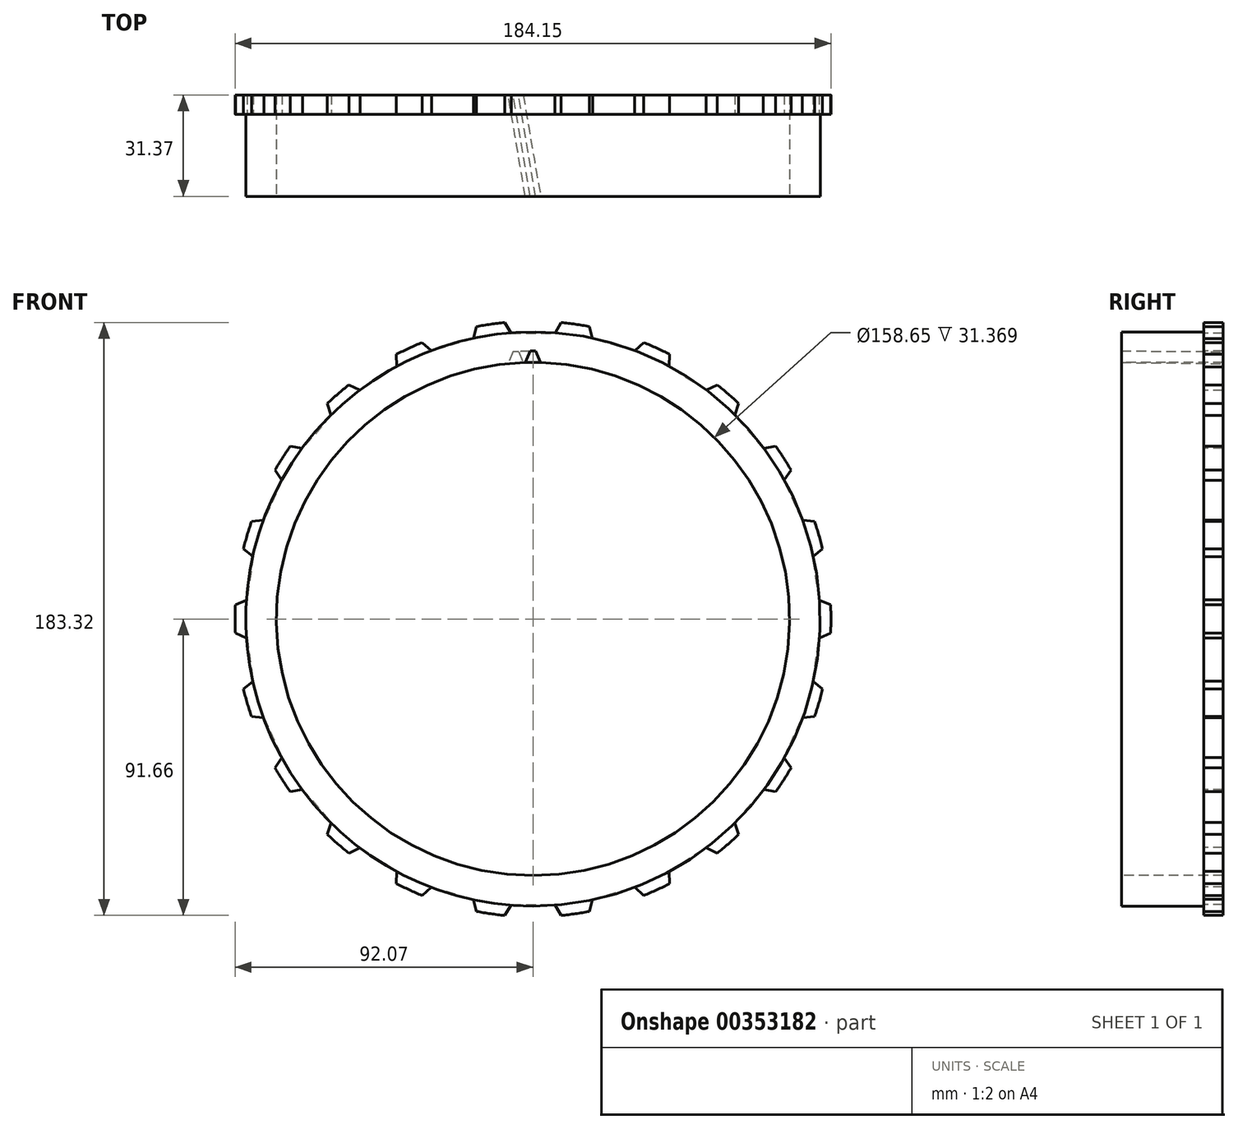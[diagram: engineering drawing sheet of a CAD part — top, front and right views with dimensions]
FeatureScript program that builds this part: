
annotation { "Feature Type Name" : "Feature", "Feature Type Description" : "" }
export const myFeature = defineFeature(function(context is Context, id is Id, definition is map)
    precondition{}
    {
        {
            var Q0;
            Q0=qCreatedBy(makeId("Front.planeOp"),FACE);
            var sketch = newSketch(context, id + "F0", { "sketchPlane" : qUnion([Q0])});
            skCircle(sketch, "E0", {"center": v(0, 0) * mm, "radius": 92.08 * mm});
            skCircle(sketch, "E1", {"center": v(0, 0) * mm, "radius": 79.32 * mm});
            skLineSegment(sketch, "E2", {"start": v(-6.74, 88.36) * mm, "end": v(0, 88.36) * mm});
            skLineSegment(sketch, "E3", {"start": v(-6.74, 88.36) * mm, "end": v(-8.72, 91.66) * mm});
            skLineSegment(sketch, "E4", {"start": v(0, 88.36) * mm, "end": v(0, 92.08) * mm});
            skLineSegment(sketch, "E5.MirrorCS", {"start": v(6.74, 88.36) * mm, "end": v(0, 88.36) * mm});
            skLineSegment(sketch, "E6.MirrorCS", {"start": v(6.74, 88.36) * mm, "end": v(8.72, 91.66) * mm});
            skLineSegment(sketch, "E7.1.0", {"start": v(-31.36, 82.88) * mm, "end": v(-34.2, 85.49) * mm});
            skLineSegment(sketch, "E7.1.1", {"start": v(-31.36, 82.88) * mm, "end": v(-24.9, 84.78) * mm});
            skLineSegment(sketch, "E7.1.2", {"start": v(-18.42, 86.68) * mm, "end": v(-24.9, 84.78) * mm});
            skLineSegment(sketch, "E7.1.3", {"start": v(-18.42, 86.68) * mm, "end": v(-17.45, 90.4) * mm});
            skLineSegment(sketch, "E7.2.0", {"start": v(-53.44, 70.69) * mm, "end": v(-56.9, 72.4) * mm});
            skLineSegment(sketch, "E7.2.1", {"start": v(-53.44, 70.69) * mm, "end": v(-47.77, 74.33) * mm});
            skLineSegment(sketch, "E7.2.2", {"start": v(-42.1, 77.98) * mm, "end": v(-47.77, 74.33) * mm});
            skLineSegment(sketch, "E7.2.3", {"start": v(-42.1, 77.98) * mm, "end": v(-42.22, 81.83) * mm});
            skLineSegment(sketch, "E7.3.0", {"start": v(-71.2, 52.77) * mm, "end": v(-74.99, 53.43) * mm});
            skLineSegment(sketch, "E7.3.1", {"start": v(-71.2, 52.77) * mm, "end": v(-66.78, 57.86) * mm});
            skLineSegment(sketch, "E7.3.2", {"start": v(-62.36, 62.96) * mm, "end": v(-66.78, 57.86) * mm});
            skLineSegment(sketch, "E7.3.3", {"start": v(-62.36, 62.96) * mm, "end": v(-63.56, 66.62) * mm});
            skLineSegment(sketch, "E7.4.0", {"start": v(-83.18, 30.57) * mm, "end": v(-87, 30.14) * mm});
            skLineSegment(sketch, "E7.4.1", {"start": v(-83.18, 30.57) * mm, "end": v(-80.37, 36.7) * mm});
            skLineSegment(sketch, "E7.4.2", {"start": v(-77.57, 42.84) * mm, "end": v(-80.37, 36.7) * mm});
            skLineSegment(sketch, "E7.4.3", {"start": v(-77.57, 42.84) * mm, "end": v(-79.75, 46.01) * mm});
            skLineSegment(sketch, "E7.5.0", {"start": v(-88.42, 5.9) * mm, "end": v(-91.97, 4.4) * mm});
            skLineSegment(sketch, "E7.5.1", {"start": v(-88.42, 5.9) * mm, "end": v(-87.46, 12.57) * mm});
            skLineSegment(sketch, "E7.5.2", {"start": v(-86.5, 19.25) * mm, "end": v(-87.46, 12.57) * mm});
            skLineSegment(sketch, "E7.5.3", {"start": v(-86.5, 19.25) * mm, "end": v(-89.49, 21.68) * mm});
            skLineSegment(sketch, "E7.6.0", {"start": v(-86.5, -19.25) * mm, "end": v(-89.49, -21.68) * mm});
            skLineSegment(sketch, "E7.6.1", {"start": v(-86.5, -19.25) * mm, "end": v(-87.46, -12.57) * mm});
            skLineSegment(sketch, "E7.6.2", {"start": v(-88.42, -5.9) * mm, "end": v(-87.46, -12.57) * mm});
            skLineSegment(sketch, "E7.6.3", {"start": v(-88.42, -5.9) * mm, "end": v(-91.97, -4.4) * mm});
            skLineSegment(sketch, "E7.7.0", {"start": v(-77.57, -42.84) * mm, "end": v(-79.75, -46.01) * mm});
            skLineSegment(sketch, "E7.7.1", {"start": v(-77.57, -42.84) * mm, "end": v(-80.37, -36.7) * mm});
            skLineSegment(sketch, "E7.7.2", {"start": v(-83.18, -30.57) * mm, "end": v(-80.37, -36.7) * mm});
            skLineSegment(sketch, "E7.7.3", {"start": v(-83.18, -30.57) * mm, "end": v(-87, -30.14) * mm});
            skLineSegment(sketch, "E7.8.0", {"start": v(-62.36, -62.96) * mm, "end": v(-63.56, -66.62) * mm});
            skLineSegment(sketch, "E7.8.1", {"start": v(-62.36, -62.96) * mm, "end": v(-66.78, -57.86) * mm});
            skLineSegment(sketch, "E7.8.2", {"start": v(-71.2, -52.77) * mm, "end": v(-66.78, -57.86) * mm});
            skLineSegment(sketch, "E7.8.3", {"start": v(-71.2, -52.77) * mm, "end": v(-74.99, -53.43) * mm});
            skLineSegment(sketch, "E7.9.0", {"start": v(-42.1, -77.98) * mm, "end": v(-42.22, -81.83) * mm});
            skLineSegment(sketch, "E7.9.1", {"start": v(-42.1, -77.98) * mm, "end": v(-47.77, -74.33) * mm});
            skLineSegment(sketch, "E7.9.2", {"start": v(-53.44, -70.69) * mm, "end": v(-47.77, -74.33) * mm});
            skLineSegment(sketch, "E7.9.3", {"start": v(-53.44, -70.69) * mm, "end": v(-56.9, -72.4) * mm});
            skLineSegment(sketch, "E7.10.0", {"start": v(-18.42, -86.68) * mm, "end": v(-17.45, -90.4) * mm});
            skLineSegment(sketch, "E7.10.1", {"start": v(-18.42, -86.68) * mm, "end": v(-24.9, -84.78) * mm});
            skLineSegment(sketch, "E7.10.2", {"start": v(-31.36, -82.88) * mm, "end": v(-24.9, -84.78) * mm});
            skLineSegment(sketch, "E7.10.3", {"start": v(-31.36, -82.88) * mm, "end": v(-34.2, -85.49) * mm});
            skLineSegment(sketch, "E7.11.0", {"start": v(6.74, -88.36) * mm, "end": v(8.72, -91.66) * mm});
            skLineSegment(sketch, "E7.11.1", {"start": v(6.74, -88.36) * mm, "end": v(0, -88.36) * mm});
            skLineSegment(sketch, "E7.11.2", {"start": v(-6.74, -88.36) * mm, "end": v(0, -88.36) * mm});
            skLineSegment(sketch, "E7.11.3", {"start": v(-6.74, -88.36) * mm, "end": v(-8.72, -91.66) * mm});
            skLineSegment(sketch, "E7.12.0", {"start": v(31.36, -82.88) * mm, "end": v(34.2, -85.49) * mm});
            skLineSegment(sketch, "E7.12.1", {"start": v(31.36, -82.88) * mm, "end": v(24.9, -84.78) * mm});
            skLineSegment(sketch, "E7.12.2", {"start": v(18.42, -86.68) * mm, "end": v(24.9, -84.78) * mm});
            skLineSegment(sketch, "E7.12.3", {"start": v(18.42, -86.68) * mm, "end": v(17.45, -90.4) * mm});
            skLineSegment(sketch, "E7.13.0", {"start": v(53.44, -70.69) * mm, "end": v(56.9, -72.4) * mm});
            skLineSegment(sketch, "E7.13.1", {"start": v(53.44, -70.69) * mm, "end": v(47.77, -74.33) * mm});
            skLineSegment(sketch, "E7.13.2", {"start": v(42.1, -77.98) * mm, "end": v(47.77, -74.33) * mm});
            skLineSegment(sketch, "E7.13.3", {"start": v(42.1, -77.98) * mm, "end": v(42.22, -81.83) * mm});
            skLineSegment(sketch, "E7.14.0", {"start": v(71.2, -52.77) * mm, "end": v(74.99, -53.43) * mm});
            skLineSegment(sketch, "E7.14.1", {"start": v(71.2, -52.77) * mm, "end": v(66.78, -57.86) * mm});
            skLineSegment(sketch, "E7.14.2", {"start": v(62.36, -62.96) * mm, "end": v(66.78, -57.86) * mm});
            skLineSegment(sketch, "E7.14.3", {"start": v(62.36, -62.96) * mm, "end": v(63.56, -66.62) * mm});
            skLineSegment(sketch, "E7.15.0", {"start": v(83.18, -30.57) * mm, "end": v(87, -30.14) * mm});
            skLineSegment(sketch, "E7.15.1", {"start": v(83.18, -30.57) * mm, "end": v(80.37, -36.7) * mm});
            skLineSegment(sketch, "E7.15.2", {"start": v(77.57, -42.84) * mm, "end": v(80.37, -36.7) * mm});
            skLineSegment(sketch, "E7.15.3", {"start": v(77.57, -42.84) * mm, "end": v(79.75, -46.01) * mm});
            skLineSegment(sketch, "E7.16.0", {"start": v(88.42, -5.9) * mm, "end": v(91.97, -4.4) * mm});
            skLineSegment(sketch, "E7.16.1", {"start": v(88.42, -5.9) * mm, "end": v(87.46, -12.57) * mm});
            skLineSegment(sketch, "E7.16.2", {"start": v(86.5, -19.25) * mm, "end": v(87.46, -12.57) * mm});
            skLineSegment(sketch, "E7.16.3", {"start": v(86.5, -19.25) * mm, "end": v(89.49, -21.68) * mm});
            skLineSegment(sketch, "E7.17.0", {"start": v(86.5, 19.25) * mm, "end": v(89.49, 21.68) * mm});
            skLineSegment(sketch, "E7.17.1", {"start": v(86.5, 19.25) * mm, "end": v(87.46, 12.57) * mm});
            skLineSegment(sketch, "E7.17.2", {"start": v(88.42, 5.9) * mm, "end": v(87.46, 12.57) * mm});
            skLineSegment(sketch, "E7.17.3", {"start": v(88.42, 5.9) * mm, "end": v(91.97, 4.4) * mm});
            skLineSegment(sketch, "E7.18.0", {"start": v(77.57, 42.84) * mm, "end": v(79.75, 46.01) * mm});
            skLineSegment(sketch, "E7.18.1", {"start": v(77.57, 42.84) * mm, "end": v(80.37, 36.7) * mm});
            skLineSegment(sketch, "E7.18.2", {"start": v(83.18, 30.57) * mm, "end": v(80.37, 36.7) * mm});
            skLineSegment(sketch, "E7.18.3", {"start": v(83.18, 30.57) * mm, "end": v(87, 30.14) * mm});
            skLineSegment(sketch, "E7.19.0", {"start": v(62.36, 62.96) * mm, "end": v(63.56, 66.62) * mm});
            skLineSegment(sketch, "E7.19.1", {"start": v(62.36, 62.96) * mm, "end": v(66.78, 57.86) * mm});
            skLineSegment(sketch, "E7.19.2", {"start": v(71.2, 52.77) * mm, "end": v(66.78, 57.86) * mm});
            skLineSegment(sketch, "E7.19.3", {"start": v(71.2, 52.77) * mm, "end": v(74.99, 53.43) * mm});
            skLineSegment(sketch, "E7.20.0", {"start": v(42.1, 77.98) * mm, "end": v(42.22, 81.83) * mm});
            skLineSegment(sketch, "E7.20.1", {"start": v(42.1, 77.98) * mm, "end": v(47.77, 74.33) * mm});
            skLineSegment(sketch, "E7.20.2", {"start": v(53.44, 70.69) * mm, "end": v(47.77, 74.33) * mm});
            skLineSegment(sketch, "E7.20.3", {"start": v(53.44, 70.69) * mm, "end": v(56.9, 72.4) * mm});
            skLineSegment(sketch, "E7.21.0", {"start": v(18.42, 86.68) * mm, "end": v(17.45, 90.4) * mm});
            skLineSegment(sketch, "E7.21.1", {"start": v(18.42, 86.68) * mm, "end": v(24.9, 84.78) * mm});
            skLineSegment(sketch, "E7.21.2", {"start": v(31.36, 82.88) * mm, "end": v(24.9, 84.78) * mm});
            skLineSegment(sketch, "E7.21.3", {"start": v(31.36, 82.88) * mm, "end": v(34.2, 85.49) * mm});
            skSolve(sketch);
        }
        {
            var Q0;
            Q0=makeQuery(id+"F0.imprint","IMPRINT",FACE,{"disambiguationData":[TD([[makeQuery(id+"F0.imprint","IMPRINT",EDGE,{"derivedFrom":sQuery(id+"F0.wireOp",EDGE,"E1")}),-1.0]])]});
            extrude(context, id + "F1", {"entities" : qUnion([Q0]), "oppositeDirection" : true, "depth" : 5.97 * mm});
        }
        {
            var Q0;
            Q0=qCreatedBy(makeId("Front.planeOp"),FACE);
            var sketch = newSketch(context, id + "F2", { "sketchPlane" : qUnion([Q0])});
            skCircle(sketch, "E8", {"center": v(0, 0) * mm, "radius": 88.77 * mm});
            skCircle(sketch, "E9", {"center": v(0, 0) * mm, "radius": 79.32 * mm});
            skSolve(sketch);
        }
        {
            var Q0;
            Q0=makeQuery(id+"F2.imprint","IMPRINT",FACE,{"disambiguationData":[TD([[makeQuery(id+"F2.imprint","IMPRINT",EDGE,{"derivedFrom":sQuery(id+"F2.wireOp",EDGE,"E8")}),1.0]])]});
            extrude(context, id + "F3", {"entities" : qUnion([Q0]), "operationType" : NewBodyOperationType.ADD, "depth" : 25.4 * mm});
        }
        {
            var Q0;
            Q0=makeQuery(id+"F3.opExtrude","CAP_FACE",FACE,{"disambiguationData":[OSD([sQuery(id+"F2.wireOp",EDGE,"E8"),sQuery(id+"F2.wireOp",EDGE,"E9")])],"isStart":false});
            var sketch = newSketch(context, id + "F4", { "sketchPlane" : qUnion([Q0])});
            skCircle(sketch, "E10", {"center": v(0, 0) * mm, "radius": 82.88 * mm});
            skLineSegment(sketch, "E11", {"start": v(0, 82.88) * mm, "end": v(0, 95.13) * mm, "construction": true});
            skLineSegment(sketch, "E12.0", {"start": v(0.84, 82.88) * mm, "end": v(0.84, 95.13) * mm, "construction": true});
            skLineSegment(sketch, "E13.0", {"start": v(2.36, 0) * mm, "end": v(2.36, 95.13) * mm, "construction": true});
            skLineSegment(sketch, "E14", {"start": v(0.84, 82.88) * mm, "end": v(3.1, 77.53) * mm});
            skLineSegment(sketch, "E15.MirrorCS", {"start": v(-0.84, 82.88) * mm, "end": v(-3.1, 77.53) * mm});
            skPoint(sketch, "E16.orphan", {"position": v(-2.36, 79.29) * mm});
            skLineSegment(sketch, "E17", {"start": v(-3.1, 77.53) * mm, "end": v(3.1, 77.53) * mm});
            skPoint(sketch, "E18.orphan", {"position": v(2.36, 79.29) * mm});
            skSolve(sketch);
        }
        {
            var Q0;
            Q0=makeQuery(id+"F1.opExtrude","CAP_FACE",FACE,{"disambiguationData":[OSD([sQuery(id+"F0.wireOp",EDGE,"E0"),sQuery(id+"F0.wireOp",EDGE,"E1"),sQuery(id+"F0.wireOp",EDGE,"E2"),sQuery(id+"F0.wireOp",EDGE,"E3"),sQuery(id+"F0.wireOp",EDGE,"E5.MirrorCS"),sQuery(id+"F0.wireOp",EDGE,"E6.MirrorCS"),sQuery(id+"F0.wireOp",EDGE,"E7.1.0"),sQuery(id+"F0.wireOp",EDGE,"E7.1.1"),sQuery(id+"F0.wireOp",EDGE,"E7.1.2"),sQuery(id+"F0.wireOp",EDGE,"E7.1.3"),sQuery(id+"F0.wireOp",EDGE,"E7.2.0"),sQuery(id+"F0.wireOp",EDGE,"E7.2.1"),sQuery(id+"F0.wireOp",EDGE,"E7.2.2"),sQuery(id+"F0.wireOp",EDGE,"E7.2.3"),sQuery(id+"F0.wireOp",EDGE,"E7.3.0"),sQuery(id+"F0.wireOp",EDGE,"E7.3.1"),sQuery(id+"F0.wireOp",EDGE,"E7.3.2"),sQuery(id+"F0.wireOp",EDGE,"E7.3.3"),sQuery(id+"F0.wireOp",EDGE,"E7.4.0"),sQuery(id+"F0.wireOp",EDGE,"E7.4.1"),sQuery(id+"F0.wireOp",EDGE,"E7.4.2"),sQuery(id+"F0.wireOp",EDGE,"E7.4.3"),sQuery(id+"F0.wireOp",EDGE,"E7.5.0"),sQuery(id+"F0.wireOp",EDGE,"E7.5.1"),sQuery(id+"F0.wireOp",EDGE,"E7.5.2"),sQuery(id+"F0.wireOp",EDGE,"E7.5.3"),sQuery(id+"F0.wireOp",EDGE,"E7.6.0"),sQuery(id+"F0.wireOp",EDGE,"E7.6.1"),sQuery(id+"F0.wireOp",EDGE,"E7.6.2"),sQuery(id+"F0.wireOp",EDGE,"E7.6.3"),sQuery(id+"F0.wireOp",EDGE,"E7.7.0"),sQuery(id+"F0.wireOp",EDGE,"E7.7.1"),sQuery(id+"F0.wireOp",EDGE,"E7.7.2"),sQuery(id+"F0.wireOp",EDGE,"E7.7.3"),sQuery(id+"F0.wireOp",EDGE,"E7.8.0"),sQuery(id+"F0.wireOp",EDGE,"E7.8.1"),sQuery(id+"F0.wireOp",EDGE,"E7.8.2"),sQuery(id+"F0.wireOp",EDGE,"E7.8.3"),sQuery(id+"F0.wireOp",EDGE,"E7.9.0"),sQuery(id+"F0.wireOp",EDGE,"E7.9.1"),sQuery(id+"F0.wireOp",EDGE,"E7.9.2"),sQuery(id+"F0.wireOp",EDGE,"E7.9.3"),sQuery(id+"F0.wireOp",EDGE,"E7.10.0"),sQuery(id+"F0.wireOp",EDGE,"E7.10.1"),sQuery(id+"F0.wireOp",EDGE,"E7.10.2"),sQuery(id+"F0.wireOp",EDGE,"E7.10.3"),sQuery(id+"F0.wireOp",EDGE,"E7.11.0"),sQuery(id+"F0.wireOp",EDGE,"E7.11.1"),sQuery(id+"F0.wireOp",EDGE,"E7.11.2"),sQuery(id+"F0.wireOp",EDGE,"E7.11.3"),sQuery(id+"F0.wireOp",EDGE,"E7.12.0"),sQuery(id+"F0.wireOp",EDGE,"E7.12.1"),sQuery(id+"F0.wireOp",EDGE,"E7.12.2"),sQuery(id+"F0.wireOp",EDGE,"E7.12.3"),sQuery(id+"F0.wireOp",EDGE,"E7.13.0"),sQuery(id+"F0.wireOp",EDGE,"E7.13.1"),sQuery(id+"F0.wireOp",EDGE,"E7.13.2"),sQuery(id+"F0.wireOp",EDGE,"E7.13.3"),sQuery(id+"F0.wireOp",EDGE,"E7.14.0"),sQuery(id+"F0.wireOp",EDGE,"E7.14.1"),sQuery(id+"F0.wireOp",EDGE,"E7.14.2"),sQuery(id+"F0.wireOp",EDGE,"E7.14.3"),sQuery(id+"F0.wireOp",EDGE,"E7.15.0"),sQuery(id+"F0.wireOp",EDGE,"E7.15.1"),sQuery(id+"F0.wireOp",EDGE,"E7.15.2"),sQuery(id+"F0.wireOp",EDGE,"E7.15.3"),sQuery(id+"F0.wireOp",EDGE,"E7.16.0"),sQuery(id+"F0.wireOp",EDGE,"E7.16.1"),sQuery(id+"F0.wireOp",EDGE,"E7.16.2"),sQuery(id+"F0.wireOp",EDGE,"E7.16.3"),sQuery(id+"F0.wireOp",EDGE,"E7.17.0"),sQuery(id+"F0.wireOp",EDGE,"E7.17.1"),sQuery(id+"F0.wireOp",EDGE,"E7.17.2"),sQuery(id+"F0.wireOp",EDGE,"E7.17.3"),sQuery(id+"F0.wireOp",EDGE,"E7.18.0"),sQuery(id+"F0.wireOp",EDGE,"E7.18.1"),sQuery(id+"F0.wireOp",EDGE,"E7.18.2"),sQuery(id+"F0.wireOp",EDGE,"E7.18.3"),sQuery(id+"F0.wireOp",EDGE,"E7.19.0"),sQuery(id+"F0.wireOp",EDGE,"E7.19.1"),sQuery(id+"F0.wireOp",EDGE,"E7.19.2"),sQuery(id+"F0.wireOp",EDGE,"E7.19.3"),sQuery(id+"F0.wireOp",EDGE,"E7.20.0"),sQuery(id+"F0.wireOp",EDGE,"E7.20.1"),sQuery(id+"F0.wireOp",EDGE,"E7.20.2"),sQuery(id+"F0.wireOp",EDGE,"E7.20.3"),sQuery(id+"F0.wireOp",EDGE,"E7.21.0"),sQuery(id+"F0.wireOp",EDGE,"E7.21.1"),sQuery(id+"F0.wireOp",EDGE,"E7.21.2"),sQuery(id+"F0.wireOp",EDGE,"E7.21.3")])],"isStart":false});
            var sketch = newSketch(context, id + "F5", { "sketchPlane" : qUnion([Q0])});
            skLineSegment(sketch, "E19", {"start": v(0, 0) * mm, "end": v(0, 105.24) * mm});
            skLineSegment(sketch, "E20", {"start": v(0, 0) * mm, "end": v(13.1, 204.13) * mm});
            skPoint(sketch, "E20.endSnap0", {"position": v(13.1, 91.14) * mm});
            skLineSegment(sketch, "E21.0", {"start": v(-0.84, 0.05) * mm, "end": v(12.27, 204.18) * mm});
            skLineSegment(sketch, "E22.0", {"start": v(-2.36, 0.15) * mm, "end": v(10.75, 204.28) * mm});
            skCircle(sketch, "E23", {"center": v(0, 0) * mm, "radius": 82.88 * mm});
            skCircle(sketch, "E24", {"center": v(0, 0) * mm, "radius": 78.56 * mm});
            skLineSegment(sketch, "E25", {"start": v(4.47, 82.76) * mm, "end": v(2.67, 78.51) * mm});
            skLineSegment(sketch, "E26.MirrorCS", {"start": v(6.15, 82.65) * mm, "end": v(7.39, 78.2) * mm});
            skPoint(sketch, "E27.orphan", {"position": v(7.39, 78.2) * mm});
            skSolve(sketch);
        }
        {
            var Q0;
            Q0=sQuery(id+"F5.wireOp",VERTEX,"E26.MirrorCS.start");
            var Q1;
            Q1=sQuery(id+"F4.wireOp",VERTEX,"E15.MirrorCS.start");
            var Q2;
            Q2=sQuery(id+"F4.wireOp",VERTEX,"E14.start");
            cPlane(context, id + "F6", {"entities" : qUnion([Q0, Q1, Q2]), "cplaneType" : CPlaneType.THREE_POINT, "offset" : 25.4 * mm, "width" : 152.4 * mm, "height" : 152.4 * mm});
        }
        {
            var Q0;
            Q0=qCreatedBy(id+"F6.planeOp",FACE);
            var sketch = newSketch(context, id + "F7", { "sketchPlane" : qUnion([Q0])});
            skPoint(sketch, "E28.0", {"position": v(-6.15, -5.38) * mm});
            skPoint(sketch, "E29.0", {"position": v(-0.84, 26) * mm});
            skLineSegment(sketch, "E30", {"start": v(-0.84, 26) * mm, "end": v(-6.15, -5.38) * mm});
            skSolve(sketch);
        }
        {
            var Q0;
            {var subQ0=sQuery(id+"F4.wireOp",EDGE,"E17");Q0=makeQuery(id+"F4.imprint","IMPRINT",FACE,{"disambiguationData":[TD([[makeQuery(id+"F4.imprint","IMPRINT",EDGE,{"derivedFrom":subQ0}),1.0]])]});}
            var Q1;
            {var subQ0=sQuery(id+"F4.wireOp",EDGE,"E14");var subQ1=sQuery(id+"F4.wireOp",EDGE,"E10");var subQ2=makeQuery(id+"F4.imprint","INTERSECT",VERTEX,{"derivedFrom":[subQ1,subQ0]});Q1=makeQuery(id+"F4.imprint","IMPRINT",FACE,{"disambiguationData":[TD([[makeQuery(id+"F4.imprint","IMPRINT",EDGE,{"disambiguationData":[TD([[subQ2,-1.0]])],"derivedFrom":subQ1}),1.0]])]});}
            var Q2;
            Q2=sQuery(id+"F7.wireOp",EDGE,"E30");
            sweep(context, id + "F8", {"operationType" : NewBodyOperationType.REMOVE, "profiles" : qUnion([Q0, Q1]), "path" : qUnion([Q2])});
        }
        {
            var Q0;
            Q0=qCreatedBy(makeId("Right.planeOp"),FACE);
            var sketch = newSketch(context, id + "F9", { "sketchPlane" : qUnion([Q0])});
            skLineSegment(sketch, "E31", {"start": v(0, 0) * mm, "end": v(77.7, 0) * mm});
            skSolve(sketch);
        }
    });
